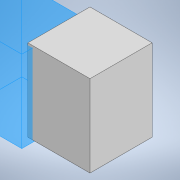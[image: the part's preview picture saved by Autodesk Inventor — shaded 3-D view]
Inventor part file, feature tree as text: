
AUTODESK INVENTOR PART (.ipt)
format: ipt  version: 2022 (Build 260153000, 153)  size: 88,064 bytes
history: native  units: mm
features: extrude x1, sketch x1
ambient origin geometry x8: Origin, YZ Plane, XZ Plane, XY Plane, X Axis, Y Axis, Z Axis, Center Point
bodies: Solid1 (feature_tree)
feature tree (2):
  extrude  "Extrusion1"  Depth=380.0mm
  sketch  "Sketch1"  dims[d0=380.0mm d1=380.0mm d2=180.0mm d3=180.0mm d4=500.0mm d5=0.0mm]
